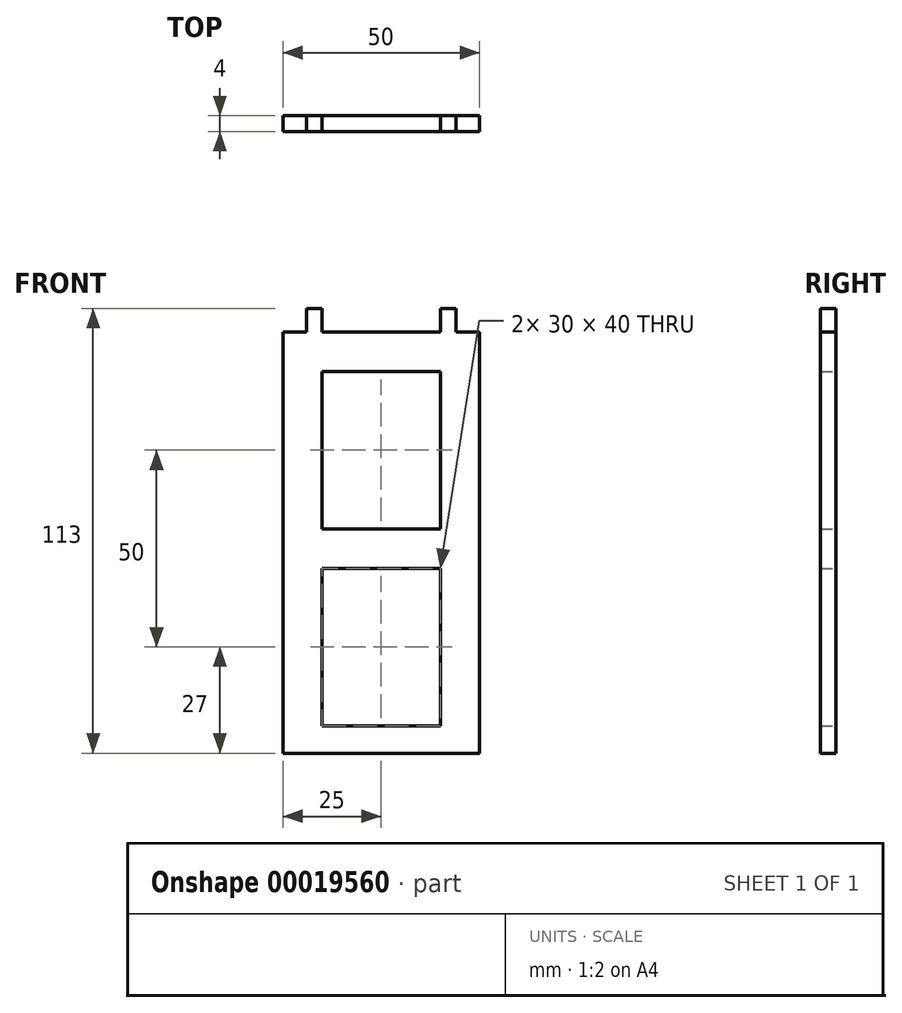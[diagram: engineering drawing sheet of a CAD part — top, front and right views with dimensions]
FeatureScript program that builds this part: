
annotation { "Feature Type Name" : "Feature", "Feature Type Description" : "" }
export const myFeature = defineFeature(function(context is Context, id is Id, definition is map)
    precondition{}
    {
        {
            var Q0;
            Q0=qCreatedBy(makeId("Front.planeOp"),FACE);
            var sketch = newSketch(context, id + "F0", { "sketchPlane" : qUnion([Q0])});
            skLineSegment(sketch, "E0.bottom", {"start": v(-25, 0) * mm, "end": v(25, 0) * mm});
            skLineSegment(sketch, "E0.top", {"start": v(-25, 107) * mm, "end": v(-19, 107) * mm});
            skLineSegment(sketch, "E0.left", {"start": v(-25, 0) * mm, "end": v(-25, 107) * mm});
            skLineSegment(sketch, "E0.right", {"start": v(25, 0) * mm, "end": v(25, 107) * mm});
            skPoint(sketch, "E1.visualSharp", {"position": v(-25, 107) * mm});
            skPoint(sketch, "E2.visualSharp", {"position": v(25, 107) * mm});
            skLineSegment(sketch, "E3", {"start": v(-25, 97) * mm, "end": v(25, 97) * mm, "construction": true});
            skLineSegment(sketch, "E4.top", {"start": v(-19, 113) * mm, "end": v(-15, 113) * mm});
            skLineSegment(sketch, "E4.left", {"start": v(-19, 107) * mm, "end": v(-19, 113) * mm});
            skLineSegment(sketch, "E4.right", {"start": v(-15, 107) * mm, "end": v(-15, 113) * mm});
            skLineSegment(sketch, "E5.top", {"start": v(15, 113) * mm, "end": v(19, 113) * mm});
            skLineSegment(sketch, "E5.left", {"start": v(15, 107) * mm, "end": v(15, 113) * mm});
            skLineSegment(sketch, "E5.right", {"start": v(19, 107) * mm, "end": v(19, 113) * mm});
            skLineSegment(sketch, "E6", {"start": v(0, 107) * mm, "end": v(0, 78.36) * mm, "construction": true});
            skLineSegment(sketch, "E7.trimOffspring", {"start": v(-15, 107) * mm, "end": v(15, 107) * mm});
            skLineSegment(sketch, "E8.trimOffspring", {"start": v(19, 107) * mm, "end": v(25, 107) * mm});
            skLineSegment(sketch, "E9.bottom", {"start": v(-15, 97) * mm, "end": v(15, 97) * mm});
            skLineSegment(sketch, "E9.top", {"start": v(-15, 57) * mm, "end": v(15, 57) * mm});
            skLineSegment(sketch, "E9.left", {"start": v(-15, 97) * mm, "end": v(-15, 57) * mm});
            skLineSegment(sketch, "E9.right", {"start": v(15, 97) * mm, "end": v(15, 57) * mm});
            skLineSegment(sketch, "E10.bottom", {"start": v(-15, 47) * mm, "end": v(15, 47) * mm});
            skLineSegment(sketch, "E10.top", {"start": v(-15, 7) * mm, "end": v(15, 7) * mm});
            skLineSegment(sketch, "E10.left", {"start": v(-15, 47) * mm, "end": v(-15, 7) * mm});
            skLineSegment(sketch, "E10.right", {"start": v(15, 47) * mm, "end": v(15, 7) * mm});
            skSolve(sketch);
        }
        {
            var Q0;
            Q0=makeQuery(id+"F0.imprint","IMPRINT",FACE,{"disambiguationData":[TD([[makeQuery(id+"F0.imprint","IMPRINT",EDGE,{"derivedFrom":sQuery(id+"F0.wireOp",EDGE,"E0.bottom")}),1.0]])]});
            extrude(context, id + "F1", {"entities" : qUnion([Q0]), "depth" : 4 * mm});
        }
    });
